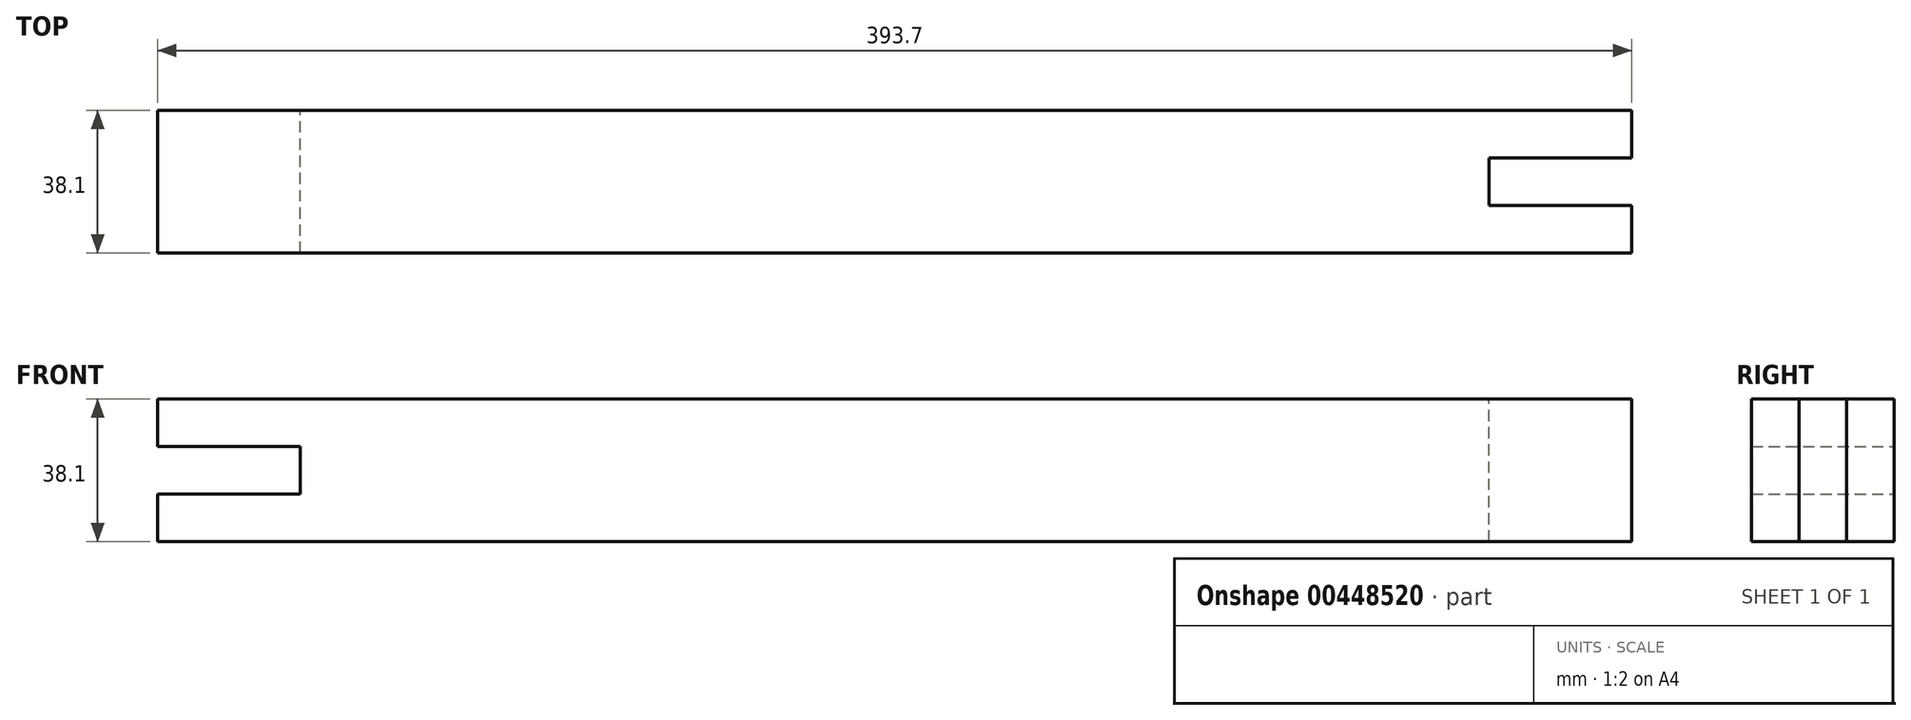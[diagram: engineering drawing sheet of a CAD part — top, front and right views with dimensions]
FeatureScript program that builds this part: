
annotation { "Feature Type Name" : "Feature", "Feature Type Description" : "" }
export const myFeature = defineFeature(function(context is Context, id is Id, definition is map)
    precondition{}
    {
        {
            var Q0;
            Q0=qCreatedBy(makeId("Front.planeOp"),FACE);
            var sketch = newSketch(context, id + "F0", { "sketchPlane" : qUnion([Q0])});
            skLineSegment(sketch, "E0.bottom", {"start": v(0, 0) * mm, "end": v(393.7, 0) * mm});
            skLineSegment(sketch, "E0.top", {"start": v(0, -38.1) * mm, "end": v(393.7, -38.1) * mm});
            skLineSegment(sketch, "E0.left", {"start": v(0, 0) * mm, "end": v(0, -12.7) * mm});
            skLineSegment(sketch, "E0.right", {"start": v(393.7, 0) * mm, "end": v(393.7, -38.1) * mm});
            skLineSegment(sketch, "E1", {"start": v(0, -12.7) * mm, "end": v(38.1, -12.7) * mm});
            skLineSegment(sketch, "E2", {"start": v(38.1, -12.7) * mm, "end": v(38.1, -25.4) * mm});
            skLineSegment(sketch, "E3", {"start": v(38.1, -25.4) * mm, "end": v(0, -25.4) * mm});
            skLineSegment(sketch, "E4.trimOffspring", {"start": v(0, -25.4) * mm, "end": v(0, -38.1) * mm});
            skSolve(sketch);
        }
        {
            var Q0;
            Q0=makeQuery(id+"F0.imprint","IMPRINT",FACE,{"disambiguationData":[TD([[makeQuery(id+"F0.imprint","IMPRINT",EDGE,{"derivedFrom":sQuery(id+"F0.wireOp",EDGE,"E0.bottom")}),-1.0]])]});
            extrude(context, id + "F1", {"entities" : qUnion([Q0]), "depth" : 38.1 * mm});
        }
        {
            var Q0;
            Q0=makeQuery(id+"F1.opExtrude","SWEPT_FACE",FACE,{"disambiguationData":[OSD([sQuery(id+"F0.wireOp",EDGE,"E0.bottom")])]});
            var sketch = newSketch(context, id + "F2", { "sketchPlane" : qUnion([Q0])});
            skLineSegment(sketch, "E5.bottom", {"start": v(393.7, -12.7) * mm, "end": v(355.6, -12.7) * mm});
            skLineSegment(sketch, "E5.top", {"start": v(393.7, -25.4) * mm, "end": v(355.6, -25.4) * mm});
            skLineSegment(sketch, "E5.left", {"start": v(393.7, -12.7) * mm, "end": v(393.7, -25.4) * mm});
            skLineSegment(sketch, "E5.right", {"start": v(355.6, -12.7) * mm, "end": v(355.6, -25.4) * mm});
            skSolve(sketch);
        }
        {
            var Q0;
            Q0=makeQuery(id+"F2.imprint","IMPRINT",FACE,{"disambiguationData":[TD([[makeQuery(id+"F2.imprint","IMPRINT",EDGE,{"derivedFrom":sQuery(id+"F2.wireOp",EDGE,"E5.bottom")}),1.0]])]});
            extrude(context, id + "F3", {"entities" : qUnion([Q0]), "operationType" : NewBodyOperationType.REMOVE, "oppositeDirection" : true, "depth" : 38.1 * mm});
        }
    });
